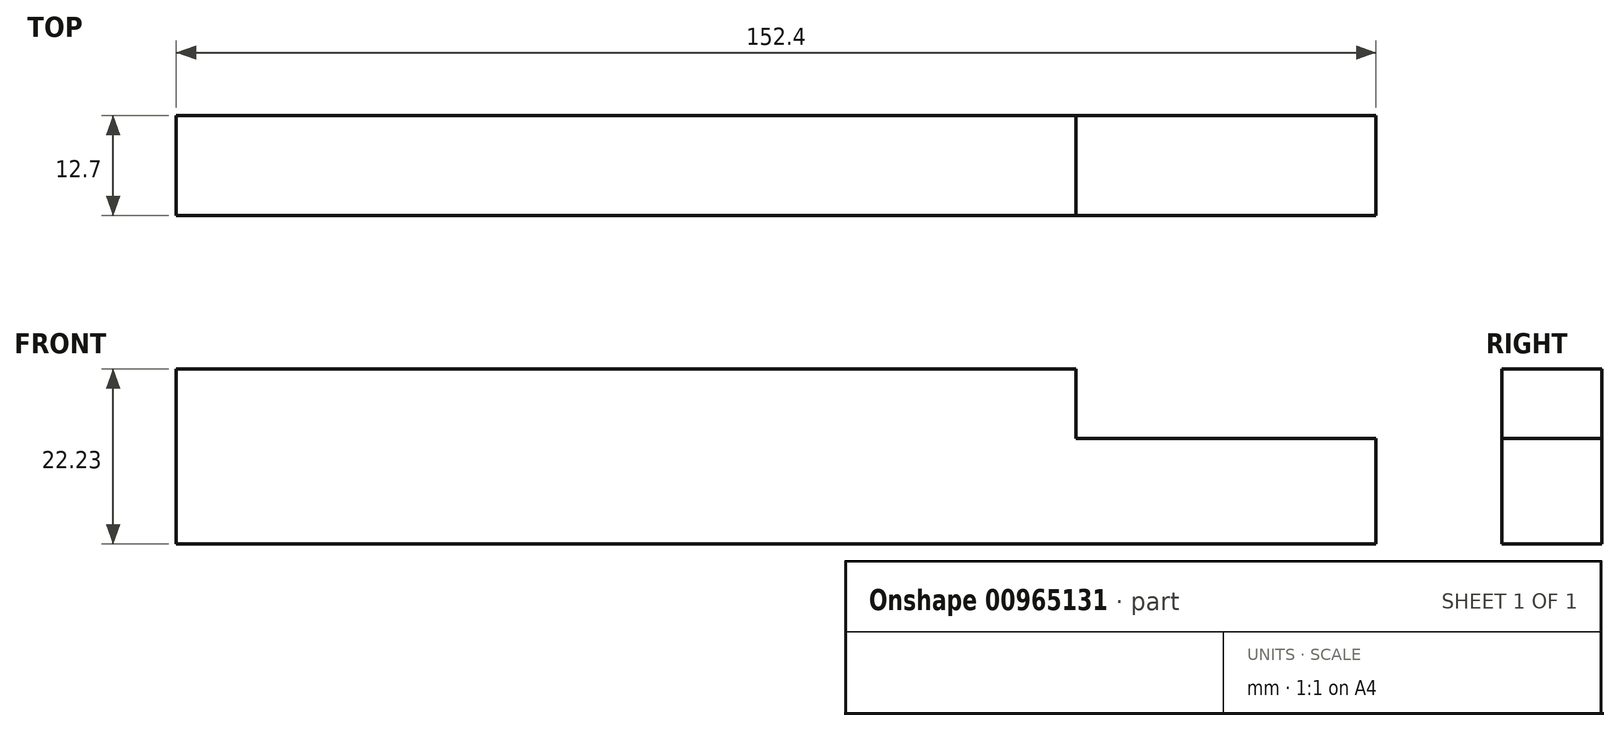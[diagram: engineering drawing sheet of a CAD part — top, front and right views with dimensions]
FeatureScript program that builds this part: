
annotation { "Feature Type Name" : "Feature", "Feature Type Description" : "" }
export const myFeature = defineFeature(function(context is Context, id is Id, definition is map)
    precondition{}
    {
        {
            var Q0;
            Q0=qCreatedBy(makeId("Front.planeOp"),FACE);
            var sketch = newSketch(context, id + "F0", { "sketchPlane" : qUnion([Q0])});
            skLineSegment(sketch, "E0", {"start": v(0, 0) * mm, "end": v(0, 13.39) * mm});
            skLineSegment(sketch, "E1", {"start": v(0, 13.39) * mm, "end": v(-38.1, 13.39) * mm});
            skLineSegment(sketch, "E2", {"start": v(-38.1, 13.39) * mm, "end": v(-38.1, 22.23) * mm});
            skLineSegment(sketch, "E3", {"start": v(-38.1, 22.23) * mm, "end": v(-152.4, 22.22) * mm});
            skLineSegment(sketch, "E4", {"start": v(-152.4, 22.22) * mm, "end": v(-152.4, 0) * mm});
            skLineSegment(sketch, "E5", {"start": v(-152.4, 0) * mm, "end": v(0, 0) * mm});
            skSolve(sketch);
        }
        {
            var Q0;
            Q0 = qSketchRegion(id + "F0", true);
            extrude(context, id + "F1", {"entities" : qUnion([Q0]), "depth" : 12.7 * mm, "offsetDistance" : 25.4 * mm});
        }
    });
